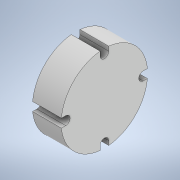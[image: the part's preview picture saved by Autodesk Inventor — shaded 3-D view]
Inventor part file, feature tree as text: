
AUTODESK INVENTOR PART (.ipt)
format: ipt  version: 2022 (Build 260153000, 153)  size: 142,336 bytes
history: native  units: mm
features: sketch x3, other x1, revolve x1, extrude x1, hole x1
ambient origin geometry x8: Origin, YZ Plane, XZ Plane, XY Plane, X Axis, Y Axis, Z Axis, Center Point
bodies: Body1 (feature_tree)
feature tree (7):
  other  "Твердое тело1"
  revolve  "Вращение1"
  extrude  "Выдавливание1"  Depth=20.0mm
  hole  "Отверстие1"  [1 undecoded]
  sketch  "Эскиз1"
  sketch  "Эскиз2"
  sketch  "Эскиз3"
note: 1 required parameter value undecoded (feature->parameter linkage not recoverable at this tier; creation-order binding heuristic only, values carry confidence <= 0.55)
